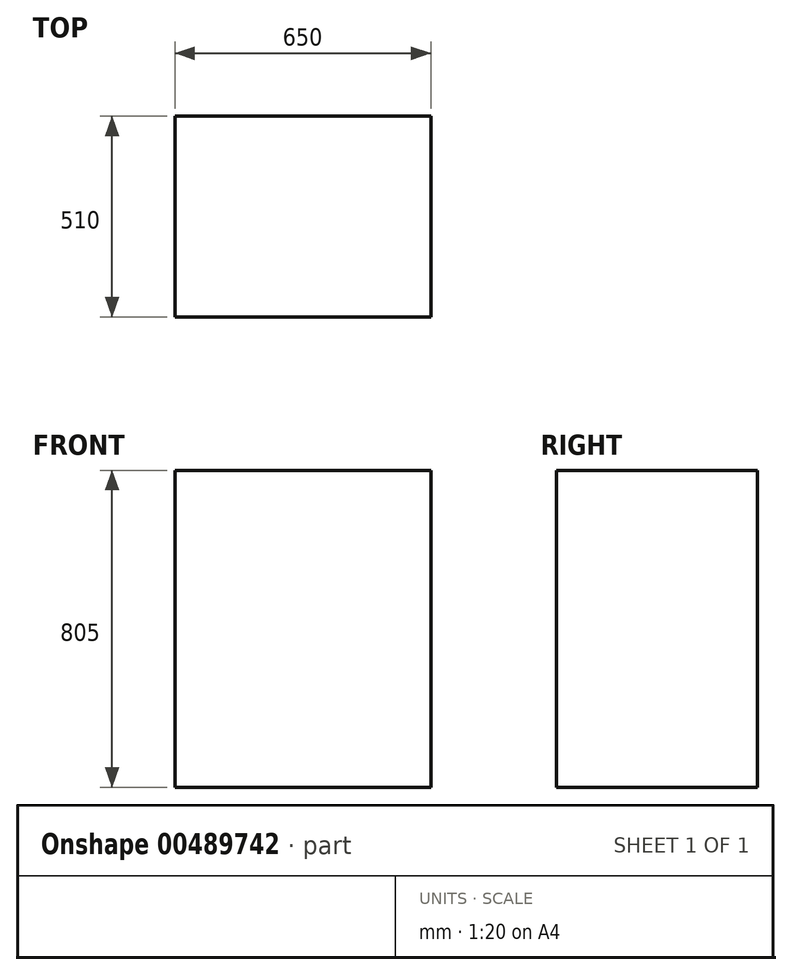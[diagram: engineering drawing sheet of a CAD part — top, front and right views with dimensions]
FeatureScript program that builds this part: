
annotation { "Feature Type Name" : "Feature", "Feature Type Description" : "" }
export const myFeature = defineFeature(function(context is Context, id is Id, definition is map)
    precondition{}
    {
        {
            var Q0;
            Q0=qCreatedBy(makeId("Top.planeOp"),FACE);
            var sketch = newSketch(context, id + "F0", { "sketchPlane" : qUnion([Q0])});
            skLineSegment(sketch, "E0.bottom", {"start": v(0, 0) * mm, "end": v(650, 0) * mm});
            skLineSegment(sketch, "E0.top", {"start": v(0, -510) * mm, "end": v(650, -510) * mm});
            skLineSegment(sketch, "E0.left", {"start": v(0, 0) * mm, "end": v(0, -510) * mm});
            skLineSegment(sketch, "E0.right", {"start": v(650, 0) * mm, "end": v(650, -510) * mm});
            skSolve(sketch);
        }
        {
            var Q0;
            Q0 = qSketchRegion(id + "F0", true);
            extrude(context, id + "F1", {"entities" : qUnion([Q0]), "depth" : 805 * mm});
        }
    });
